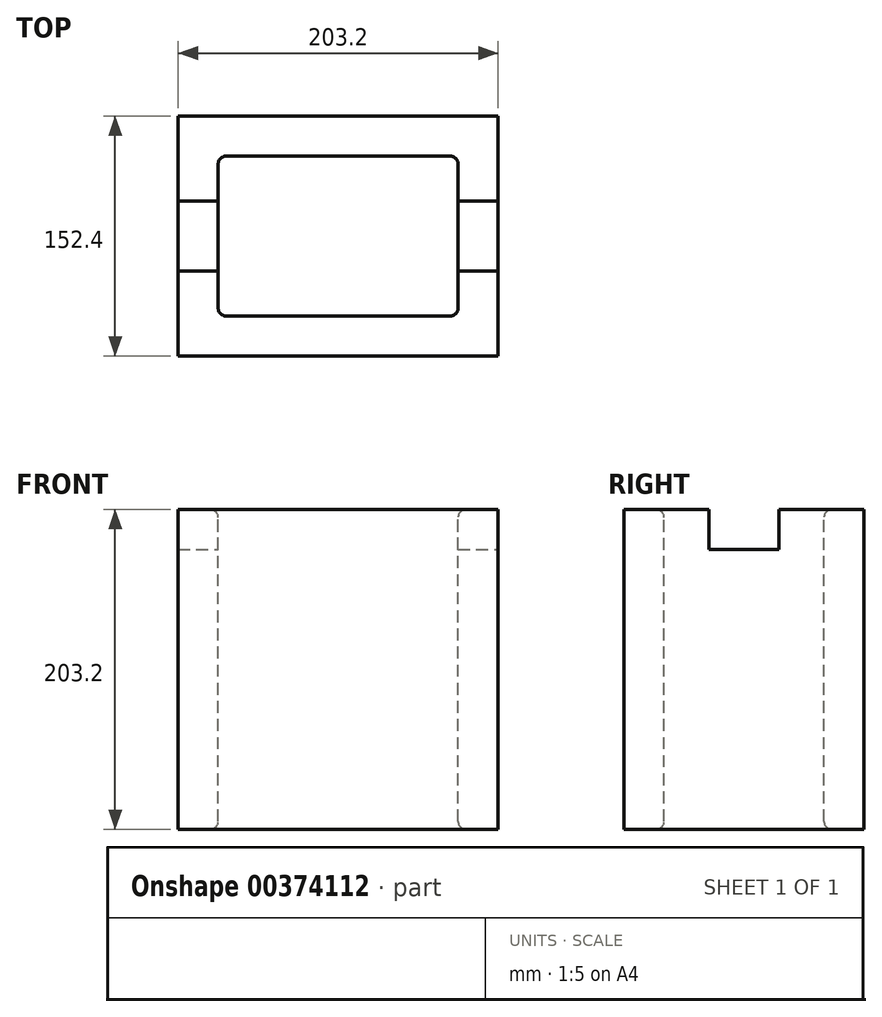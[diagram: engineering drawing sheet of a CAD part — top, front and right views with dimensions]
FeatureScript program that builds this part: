
annotation { "Feature Type Name" : "Feature", "Feature Type Description" : "" }
export const myFeature = defineFeature(function(context is Context, id is Id, definition is map)
    precondition{}
    {
        {
            var Q0;
            Q0=qCreatedBy(makeId("Top.planeOp"),FACE);
            var sketch = newSketch(context, id + "F0", { "sketchPlane" : qUnion([Q0])});
            skLineSegment(sketch, "E0.bottom", {"start": v(-101.6, 76.2) * mm, "end": v(101.6, 76.2) * mm});
            skLineSegment(sketch, "E0.top", {"start": v(-101.6, -76.2) * mm, "end": v(101.6, -76.2) * mm});
            skLineSegment(sketch, "E0.left", {"start": v(-101.6, 76.2) * mm, "end": v(-101.6, -76.2) * mm});
            skLineSegment(sketch, "E0.right", {"start": v(101.6, 76.2) * mm, "end": v(101.6, -76.2) * mm});
            skPoint(sketch, "E0.middle", {"position": v(0, 0) * mm});
            skSolve(sketch);
        }
        {
            var Q0;
            Q0 = qSketchRegion(id + "F0", true);
            extrude(context, id + "F1", {"entities" : qUnion([Q0]), "depth" : 203.2 * mm});
        }
        {
            var Q0;
            Q0=makeQuery(id+"F1.opExtrude","CAP_FACE",FACE,{"disambiguationData":[OSD([sQuery(id+"F0.wireOp",EDGE,"E0.bottom"),sQuery(id+"F0.wireOp",EDGE,"E0.top"),sQuery(id+"F0.wireOp",EDGE,"E0.left"),sQuery(id+"F0.wireOp",EDGE,"E0.right")])],"isStart":false});
            var sketch = newSketch(context, id + "F2", { "sketchPlane" : qUnion([Q0])});
            skLineSegment(sketch, "E1.bottom", {"start": v(-76.2, 50.8) * mm, "end": v(76.2, 50.8) * mm});
            skLineSegment(sketch, "E1.top", {"start": v(-76.2, -50.8) * mm, "end": v(76.2, -50.8) * mm});
            skLineSegment(sketch, "E1.left", {"start": v(-76.2, 50.8) * mm, "end": v(-76.2, -50.8) * mm});
            skLineSegment(sketch, "E1.right", {"start": v(76.2, 50.8) * mm, "end": v(76.2, -50.8) * mm});
            skPoint(sketch, "E1.middle", {"position": v(0, 0) * mm});
            skSolve(sketch);
        }
        {
            var Q0;
            Q0=makeQuery(id+"F2.imprint","IMPRINT",FACE,{"disambiguationData":[TD([[makeQuery(id+"F2.imprint","IMPRINT",EDGE,{"derivedFrom":sQuery(id+"F2.wireOp",EDGE,"E1.bottom")}),-1.0]])]});
            extrude(context, id + "F3", {"entities" : qUnion([Q0]), "operationType" : NewBodyOperationType.REMOVE, "endBound" : BoundingType.THROUGH_ALL, "oppositeDirection" : true, "depth" : 25.4 * mm});
        }
        {
            var Q0;
            Q0=makeQuery(id+"F3.boolean.opBoolean","COPY",FACE,{"derivedFrom":makeQuery(id+"F3.opExtrude","SWEPT_FACE",FACE,{"disambiguationData":[OSD([sQuery(id+"F2.wireOp",EDGE,"E1.left")])]})});
            var Q1;
            Q1=makeQuery(id+"F3.boolean.opBoolean","COPY",FACE,{"derivedFrom":makeQuery(id+"F3.opExtrude","SWEPT_FACE",FACE,{"disambiguationData":[OSD([sQuery(id+"F2.wireOp",EDGE,"E1.top")])]})});
            var Q2;
            Q2=makeQuery(id+"F3.boolean.opBoolean","COPY",FACE,{"derivedFrom":makeQuery(id+"F3.opExtrude","SWEPT_FACE",FACE,{"disambiguationData":[OSD([sQuery(id+"F2.wireOp",EDGE,"E1.right")])]})});
            var Q3;
            Q3=makeQuery(id+"F3.boolean.opBoolean","COPY",FACE,{"derivedFrom":makeQuery(id+"F3.opExtrude","SWEPT_FACE",FACE,{"disambiguationData":[OSD([sQuery(id+"F2.wireOp",EDGE,"E1.bottom")])]})});
            fillet(context, id + "F4", {"entities" : qUnion([Q0, Q1, Q2, Q3]), "radius" : 5.08 * mm, "tangentPropagation" : true, "allowEdgeOverflow" : false});
        }
        {
            var Q0;
            Q0=makeQuery(id+"F1.opExtrude","SWEPT_FACE",FACE,{"disambiguationData":[OSD([sQuery(id+"F0.wireOp",EDGE,"E0.right")])]});
            var sketch = newSketch(context, id + "F5", { "sketchPlane" : qUnion([Q0])});
            skLineSegment(sketch, "E2", {"start": v(-22.23, 203.2) * mm, "end": v(-22.23, 177.8) * mm});
            skLineSegment(sketch, "E3", {"start": v(-22.23, 177.8) * mm, "end": v(22.23, 177.8) * mm});
            skLineSegment(sketch, "E4", {"start": v(22.23, 177.8) * mm, "end": v(22.23, 203.2) * mm});
            skSolve(sketch);
        }
        {
            var Q0;
            {var subQ0=sQuery(id+"F5.wireOp",EDGE,"E2");Q0=makeQuery(id+"F5.imprint","IMPRINT",FACE,{"disambiguationData":[TD([[makeQuery(id+"F5.imprint","IMPRINT",EDGE,{"derivedFrom":subQ0}),1.0]])]});}
            var Q1;
            Q1=sQuery(id+"F5.wireOp",EDGE,"E3");
            var Q2;
            Q2=sQuery(id+"F5.wireOp",EDGE,"E2");
            var Q3;
            Q3=sQuery(id+"F5.wireOp",EDGE,"E4");
            extrude(context, id + "F6", {"entities" : qUnion([Q0]), "operationType" : NewBodyOperationType.REMOVE, "surfaceEntities" : qUnion([Q1, Q2, Q3]), "oppositeDirection" : true, "depth" : 203.2 * mm});
        }
    });
